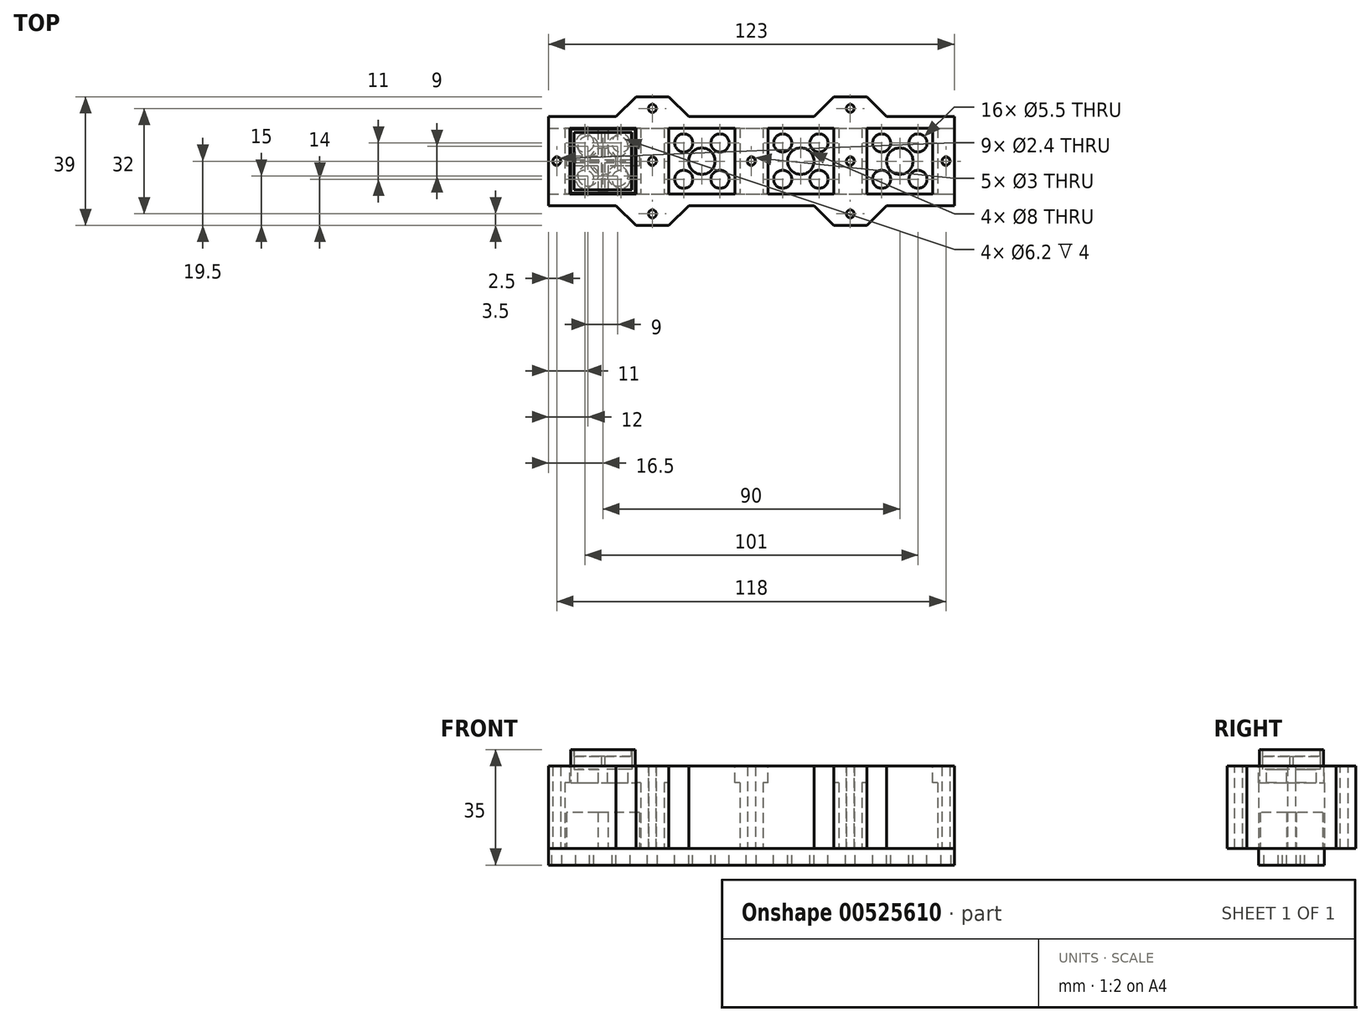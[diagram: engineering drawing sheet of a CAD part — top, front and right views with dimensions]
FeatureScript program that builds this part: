
annotation { "Feature Type Name" : "Feature", "Feature Type Description" : "" }
export const myFeature = defineFeature(function(context is Context, id is Id, definition is map)
    precondition{}
    {
        {
            var Q0;
            Q0=qCreatedBy(makeId("Top.planeOp"),FACE);
            var sketch = newSketch(context, id + "F0", { "sketchPlane" : qUnion([Q0])});
            skPoint(sketch, "E0.middle", {"position": v(0, 0) * mm});
            skLineSegment(sketch, "E1.bottom", {"start": v(9.75, -9.75) * mm, "end": v(-9.75, -9.75) * mm});
            skLineSegment(sketch, "E1.top", {"start": v(9.75, 9.75) * mm, "end": v(-9.75, 9.75) * mm});
            skLineSegment(sketch, "E1.left", {"start": v(9.75, -9.75) * mm, "end": v(9.75, 9.75) * mm});
            skLineSegment(sketch, "E1.right", {"start": v(-9.75, -9.75) * mm, "end": v(-9.75, 9.75) * mm});
            skSolve(sketch);
        }
        {
            var Q0;
            Q0=qSketchRegion(id+"F0",true);
            extrude(context, id + "F1", {"entities" : qUnion([Q0]), "depth" : 13 * mm, "offsetDistance" : 25 * mm});
        }
        {
            var Q0;
            Q0=makeQuery(id+"F1.opExtrude","CAP_FACE",FACE,{"disambiguationData":[OSD([sQuery(id+"F0.wireOp",EDGE,"E1.bottom"),sQuery(id+"F0.wireOp",EDGE,"E1.top"),sQuery(id+"F0.wireOp",EDGE,"E1.left"),sQuery(id+"F0.wireOp",EDGE,"E1.right")])],"isStart":false});
            var sketch = newSketch(context, id + "F2", { "sketchPlane" : qUnion([Q0])});
            skLineSegment(sketch, "E2.bottom", {"start": v(9.75, -9.75) * mm, "end": v(-9.75, -9.75) * mm});
            skLineSegment(sketch, "E2.top", {"start": v(9.75, 9.75) * mm, "end": v(-9.75, 9.75) * mm});
            skLineSegment(sketch, "E2.left", {"start": v(9.75, -9.75) * mm, "end": v(9.75, 9.75) * mm});
            skLineSegment(sketch, "E2.right", {"start": v(-9.75, -9.75) * mm, "end": v(-9.75, 9.75) * mm});
            skPoint(sketch, "E2.middle", {"position": v(0, 0) * mm});
            skLineSegment(sketch, "E3.bottom", {"start": v(8.75, -8.75) * mm, "end": v(-8.75, -8.75) * mm});
            skLineSegment(sketch, "E3.top", {"start": v(8.75, 8.75) * mm, "end": v(-8.75, 8.75) * mm});
            skLineSegment(sketch, "E3.left", {"start": v(8.75, -8.75) * mm, "end": v(8.75, 8.75) * mm});
            skLineSegment(sketch, "E3.right", {"start": v(-8.75, -8.75) * mm, "end": v(-8.75, 8.75) * mm});
            skSolve(sketch);
        }
        {
            var Q0;
            Q0=qSketchRegion(id+"F2",true);
            extrude(context, id + "F3", {"entities" : qUnion([Q0]), "operationType" : NewBodyOperationType.ADD, "depth" : 6 * mm, "offsetDistance" : 25 * mm});
        }
        {
            var Q0;
            Q0=makeQuery(id+"F1.opExtrude","CAP_FACE",FACE,{"disambiguationData":[OSD([sQuery(id+"F0.wireOp",EDGE,"E1.bottom"),sQuery(id+"F0.wireOp",EDGE,"E1.top"),sQuery(id+"F0.wireOp",EDGE,"E1.left"),sQuery(id+"F0.wireOp",EDGE,"E1.right")])],"isStart":false});
            var sketch = newSketch(context, id + "F4", { "sketchPlane" : qUnion([Q0])});
            skLineSegment(sketch, "E4.bottom", {"start": v(-0.5, 8.75) * mm, "end": v(0.5, 8.75) * mm});
            skLineSegment(sketch, "E4.top", {"start": v(-0.5, -8.75) * mm, "end": v(0.5, -8.75) * mm});
            skLineSegment(sketch, "E4.left", {"start": v(-0.5, 8.75) * mm, "end": v(-0.5, 0.5) * mm});
            skLineSegment(sketch, "E4.right", {"start": v(0.5, 8.75) * mm, "end": v(0.5, 0.5) * mm});
            skLineSegment(sketch, "E5.bottom", {"start": v(-8.75, 0.5) * mm, "end": v(-0.5, 0.5) * mm});
            skLineSegment(sketch, "E5.top", {"start": v(-8.75, -0.5) * mm, "end": v(-0.5, -0.5) * mm});
            skLineSegment(sketch, "E5.left", {"start": v(-8.75, 0.5) * mm, "end": v(-8.75, -0.5) * mm});
            skLineSegment(sketch, "E5.right", {"start": v(8.75, 0.5) * mm, "end": v(8.75, -0.5) * mm});
            skLineSegment(sketch, "E6.trimOffspring", {"start": v(-0.5, -0.5) * mm, "end": v(-0.5, -8.75) * mm});
            skLineSegment(sketch, "E7.trimOffspring", {"start": v(0.5, -0.5) * mm, "end": v(0.5, -8.75) * mm});
            skLineSegment(sketch, "E8.trimOffspring", {"start": v(0.5, 0.5) * mm, "end": v(8.75, 0.5) * mm});
            skLineSegment(sketch, "E9.trimOffspring", {"start": v(0.5, -0.5) * mm, "end": v(8.75, -0.5) * mm});
            skSolve(sketch);
        }
        {
            var Q0;
            Q0=qSketchRegion(id+"F4",true);
            extrude(context, id + "F5", {"entities" : qUnion([Q0]), "operationType" : NewBodyOperationType.ADD, "depth" : 4 * mm, "offsetDistance" : 25 * mm});
        }
        {
            var Q0;
            Q0=makeQuery(id+"F1.opExtrude","CAP_FACE",FACE,{"disambiguationData":[OSD([sQuery(id+"F0.wireOp",EDGE,"E1.bottom"),sQuery(id+"F0.wireOp",EDGE,"E1.top"),sQuery(id+"F0.wireOp",EDGE,"E1.left"),sQuery(id+"F0.wireOp",EDGE,"E1.right")])],"isStart":false});
            var sketch = newSketch(context, id + "F6", { "sketchPlane" : qUnion([Q0])});
            skCircle(sketch, "E10", {"center": v(-4.5, 4.5) * mm, "radius": 3.1 * mm});
            skCircle(sketch, "E11", {"center": v(-4.5, -4.5) * mm, "radius": 3.1 * mm});
            skCircle(sketch, "E12", {"center": v(4.5, 4.5) * mm, "radius": 3.1 * mm});
            skCircle(sketch, "E13", {"center": v(4.5, -4.5) * mm, "radius": 3.1 * mm});
            skSolve(sketch);
        }
        {
            var Q0;
            Q0=qSketchRegion(id+"F6",true);
            extrude(context, id + "F7", {"entities" : qUnion([Q0]), "operationType" : NewBodyOperationType.REMOVE, "oppositeDirection" : true, "depth" : 19 * mm, "offsetDistance" : 25 * mm});
        }
        {
            var Q0;
            Q0=makeQuery(id+"F1.opExtrude","CAP_FACE",FACE,{"disambiguationData":[OSD([sQuery(id+"F0.wireOp",EDGE,"E1.bottom"),sQuery(id+"F0.wireOp",EDGE,"E1.top"),sQuery(id+"F0.wireOp",EDGE,"E1.left"),sQuery(id+"F0.wireOp",EDGE,"E1.right")])],"isStart":true});
            var sketch = newSketch(context, id + "F8", { "sketchPlane" : qUnion([Q0])});
            skLineSegment(sketch, "E14.bottom", {"start": v(-9.75, -9.75) * mm, "end": v(-11.25, -9.75) * mm});
            skLineSegment(sketch, "E14.top", {"start": v(-9.75, 9.75) * mm, "end": v(-11.25, 9.75) * mm});
            skLineSegment(sketch, "E14.left", {"start": v(-9.75, -9.75) * mm, "end": v(-9.75, 9.75) * mm});
            skLineSegment(sketch, "E14.right", {"start": v(-11.25, -9.75) * mm, "end": v(-11.25, 9.75) * mm});
            skLineSegment(sketch, "E15.bottom", {"start": v(9.75, -9.75) * mm, "end": v(11.25, -9.75) * mm});
            skLineSegment(sketch, "E15.top", {"start": v(9.75, 9.75) * mm, "end": v(11.25, 9.75) * mm});
            skLineSegment(sketch, "E15.left", {"start": v(9.75, -9.75) * mm, "end": v(9.75, 9.75) * mm});
            skLineSegment(sketch, "E15.right", {"start": v(11.25, -9.75) * mm, "end": v(11.25, 9.75) * mm});
            skSolve(sketch);
        }
        {
            var Q0;
            Q0=qSketchRegion(id+"F8",true);
            extrude(context, id + "F9", {"entities" : qUnion([Q0]), "operationType" : NewBodyOperationType.ADD, "oppositeDirection" : true, "depth" : 9 * mm, "offsetDistance" : 25 * mm});
        }
        {
            var Q0;
            Q0=makeQuery(id+"F9.boolean.opBoolean","MERGE",FACE,{"derivedFrom":[makeQuery(id+"F1.opExtrude","CAP_FACE",FACE,{"disambiguationData":[OSD([sQuery(id+"F0.wireOp",EDGE,"E1.bottom"),sQuery(id+"F0.wireOp",EDGE,"E1.top"),sQuery(id+"F0.wireOp",EDGE,"E1.left"),sQuery(id+"F0.wireOp",EDGE,"E1.right")])],"isStart":true}),makeQuery(id+"F9.opExtrude","CAP_FACE",FACE,{"disambiguationData":[OSD([sQuery(id+"F8.wireOp",EDGE,"E14.bottom"),sQuery(id+"F8.wireOp",EDGE,"E14.top"),sQuery(id+"F8.wireOp",EDGE,"E14.left"),sQuery(id+"F8.wireOp",EDGE,"E14.right")])],"isStart":true}),makeQuery(id+"F9.opExtrude","CAP_FACE",FACE,{"disambiguationData":[OSD([sQuery(id+"F8.wireOp",EDGE,"E15.bottom"),sQuery(id+"F8.wireOp",EDGE,"E15.top"),sQuery(id+"F8.wireOp",EDGE,"E15.left"),sQuery(id+"F8.wireOp",EDGE,"E15.right")])],"isStart":true})]});
            var sketch = newSketch(context, id + "F10", { "sketchPlane" : qUnion([Q0])});
            skCircle(sketch, "E16", {"center": v(0, 0) * mm, "radius": 2.55 * mm});
            skSolve(sketch);
        }
        {
            var Q0;
            Q0 = qSketchRegion(id + "F10", true);
            extrude(context, id + "F11", {"entities" : qUnion([Q0]), "operationType" : NewBodyOperationType.REMOVE, "oppositeDirection" : true, "depth" : 3 * mm, "offsetDistance" : 25 * mm});
        }
        {
            var Q0;
            Q0=qCreatedBy(makeId("Top.planeOp"),FACE);
            cPlane(context, id + "F12", {"entities" : qUnion([Q0]), "cplaneType" : CPlaneType.OFFSET, "offset" : 14 * mm, "width" : 150 * mm, "height" : 150 * mm});
        }
        {
            var Q0;
            Q0=qCreatedBy(id+"F12.planeOp",FACE);
            var sketch = newSketch(context, id + "F13", { "sketchPlane" : qUnion([Q0])});
            skPoint(sketch, "E17.middle", {"position": v(0, 0) * mm});
            skLineSegment(sketch, "E18.bottom", {"start": v(10, -10) * mm, "end": v(-10, -10) * mm});
            skLineSegment(sketch, "E18.top", {"start": v(10, 10) * mm, "end": v(-10, 10) * mm});
            skLineSegment(sketch, "E18.left", {"start": v(10, -10) * mm, "end": v(10, 10) * mm});
            skLineSegment(sketch, "E18.right", {"start": v(-10, -10) * mm, "end": v(-10, 10) * mm});
            skLineSegment(sketch, "E19.bottom", {"start": v(40, -10) * mm, "end": v(20, -10) * mm});
            skLineSegment(sketch, "E19.top", {"start": v(40, 10) * mm, "end": v(20, 10) * mm});
            skLineSegment(sketch, "E19.left", {"start": v(40, -10) * mm, "end": v(40, 10) * mm});
            skLineSegment(sketch, "E19.right", {"start": v(20, -10) * mm, "end": v(20, 10) * mm});
            skPoint(sketch, "E19.middle", {"position": v(30, 0) * mm});
            skLineSegment(sketch, "E20.bottom", {"start": v(70, -10) * mm, "end": v(50, -10) * mm});
            skLineSegment(sketch, "E20.top", {"start": v(70, 10) * mm, "end": v(50, 10) * mm});
            skLineSegment(sketch, "E20.left", {"start": v(70, -10) * mm, "end": v(70, 10) * mm});
            skLineSegment(sketch, "E20.right", {"start": v(50, -10) * mm, "end": v(50, 10) * mm});
            skPoint(sketch, "E20.middle", {"position": v(60, 0) * mm});
            skLineSegment(sketch, "E21.bottom", {"start": v(100, -10) * mm, "end": v(80, -10) * mm});
            skLineSegment(sketch, "E21.top", {"start": v(100, 10) * mm, "end": v(80, 10) * mm});
            skLineSegment(sketch, "E21.left", {"start": v(100, -10) * mm, "end": v(100, 10) * mm});
            skLineSegment(sketch, "E21.right", {"start": v(80, -10) * mm, "end": v(80, 10) * mm});
            skPoint(sketch, "E21.middle", {"position": v(90, 0) * mm});
            skLineSegment(sketch, "E22.bottom", {"start": v(10, 13.5) * mm, "end": v(20, 13.5) * mm});
            skLineSegment(sketch, "E22.top", {"start": v(10, 19.5) * mm, "end": v(20, 19.5) * mm});
            skLineSegment(sketch, "E22.left", {"start": v(10, 13.5) * mm, "end": v(10, 19.5) * mm});
            skLineSegment(sketch, "E22.right", {"start": v(20, 13.5) * mm, "end": v(20, 19.5) * mm});
            skLineSegment(sketch, "E23.bottom", {"start": v(10, -13.5) * mm, "end": v(20, -13.5) * mm});
            skLineSegment(sketch, "E23.top", {"start": v(10, -19.5) * mm, "end": v(20, -19.5) * mm});
            skLineSegment(sketch, "E23.left", {"start": v(10, -13.5) * mm, "end": v(10, -19.5) * mm});
            skLineSegment(sketch, "E23.right", {"start": v(20, -13.5) * mm, "end": v(20, -19.5) * mm});
            skLineSegment(sketch, "E24.bottom", {"start": v(106.5, -13.5) * mm, "end": v(-16.5, -13.5) * mm});
            skLineSegment(sketch, "E24.top", {"start": v(106.5, 13.5) * mm, "end": v(-16.5, 13.5) * mm});
            skLineSegment(sketch, "E24.left", {"start": v(106.5, -13.5) * mm, "end": v(106.5, 13.5) * mm});
            skLineSegment(sketch, "E24.right", {"start": v(-16.5, -13.5) * mm, "end": v(-16.5, 13.5) * mm});
            skPoint(sketch, "E24.middle", {"position": v(45, 0) * mm});
            skLineSegment(sketch, "E25.bottom", {"start": v(70, 13.5) * mm, "end": v(80, 13.5) * mm});
            skLineSegment(sketch, "E25.top", {"start": v(70, 19.5) * mm, "end": v(80, 19.5) * mm});
            skLineSegment(sketch, "E25.left", {"start": v(70, 13.5) * mm, "end": v(70, 19.5) * mm});
            skLineSegment(sketch, "E25.right", {"start": v(80, 13.5) * mm, "end": v(80, 19.5) * mm});
            skLineSegment(sketch, "E26.bottom", {"start": v(70, -13.5) * mm, "end": v(80, -13.5) * mm});
            skLineSegment(sketch, "E26.top", {"start": v(70, -19.5) * mm, "end": v(80, -19.5) * mm});
            skLineSegment(sketch, "E26.left", {"start": v(70, -13.5) * mm, "end": v(70, -19.5) * mm});
            skLineSegment(sketch, "E26.right", {"start": v(80, -13.5) * mm, "end": v(80, -19.5) * mm});
            skSolve(sketch);
        }
        {
            var Q0;
            Q0=qSketchRegion(id+"F13",true);
            extrude(context, id + "F14", {"entities" : qUnion([Q0]), "oppositeDirection" : true, "depth" : 25 * mm, "offsetDistance" : 25 * mm});
        }
        {
            var Q0;
            Q0=makeQuery(id+"F14.opExtrude","CAP_FACE",FACE,{"disambiguationData":[OSD([sQuery(id+"F13.wireOp",EDGE,"E17.bottom"),sQuery(id+"F13.wireOp",EDGE,"E17.top"),sQuery(id+"F13.wireOp",EDGE,"E17.left"),sQuery(id+"F13.wireOp",EDGE,"E17.right"),sQuery(id+"F13.wireOp",EDGE,"E18.bottom"),sQuery(id+"F13.wireOp",EDGE,"E18.top"),sQuery(id+"F13.wireOp",EDGE,"E18.left"),sQuery(id+"F13.wireOp",EDGE,"E18.right")])],"isStart":false});
            var sketch = newSketch(context, id + "F15", { "sketchPlane" : qUnion([Q0])});
            skLineSegment(sketch, "E27.bottom", {"start": v(11.5, -10) * mm, "end": v(-11.5, -10) * mm});
            skLineSegment(sketch, "E27.top", {"start": v(11.5, 10) * mm, "end": v(-11.5, 10) * mm});
            skLineSegment(sketch, "E27.left", {"start": v(11.5, -10) * mm, "end": v(11.5, 10) * mm});
            skLineSegment(sketch, "E27.right", {"start": v(-11.5, -10) * mm, "end": v(-11.5, 10) * mm});
            skPoint(sketch, "E27.middle", {"position": v(0, 0) * mm});
            skLineSegment(sketch, "E28.bottom", {"start": v(41.5, -10) * mm, "end": v(18.5, -10) * mm});
            skLineSegment(sketch, "E28.top", {"start": v(41.5, 10) * mm, "end": v(18.5, 10) * mm});
            skLineSegment(sketch, "E28.left", {"start": v(41.5, -10) * mm, "end": v(41.5, 10) * mm});
            skLineSegment(sketch, "E28.right", {"start": v(18.5, -10) * mm, "end": v(18.5, 10) * mm});
            skPoint(sketch, "E28.middle", {"position": v(30, 0) * mm});
            skPoint(sketch, "E28.middle.positionSnap0", {"position": v(20, 0) * mm});
            skPoint(sketch, "E28.middle.positionSnap1", {"position": v(30, 10) * mm});
            skPoint(sketch, "E28.centerSnap0", {"position": v(20, 0) * mm});
            skPoint(sketch, "E28.centerSnap1", {"position": v(30, 10) * mm});
            skLineSegment(sketch, "E29.bottom", {"start": v(71.5, -10) * mm, "end": v(48.5, -10) * mm});
            skLineSegment(sketch, "E29.top", {"start": v(71.5, 10) * mm, "end": v(48.5, 10) * mm});
            skLineSegment(sketch, "E29.left", {"start": v(71.5, -10) * mm, "end": v(71.5, 10) * mm});
            skLineSegment(sketch, "E29.right", {"start": v(48.5, -10) * mm, "end": v(48.5, 10) * mm});
            skPoint(sketch, "E29.middle", {"position": v(60, 0) * mm});
            skPoint(sketch, "E29.middle.positionSnap0", {"position": v(50, 0) * mm});
            skPoint(sketch, "E29.middle.positionSnap1", {"position": v(60, 10) * mm});
            skPoint(sketch, "E29.centerSnap0", {"position": v(50, 0) * mm});
            skPoint(sketch, "E29.centerSnap1", {"position": v(60, 10) * mm});
            skLineSegment(sketch, "E30.bottom", {"start": v(101.5, -10) * mm, "end": v(78.5, -10) * mm});
            skLineSegment(sketch, "E30.top", {"start": v(101.5, 10) * mm, "end": v(78.5, 10) * mm});
            skLineSegment(sketch, "E30.left", {"start": v(101.5, -10) * mm, "end": v(101.5, 10) * mm});
            skLineSegment(sketch, "E30.right", {"start": v(78.5, -10) * mm, "end": v(78.5, 10) * mm});
            skPoint(sketch, "E30.middle", {"position": v(90, 0) * mm});
            skPoint(sketch, "E30.middle.positionSnap0", {"position": v(90, 10) * mm});
            skPoint(sketch, "E30.centerSnap0", {"position": v(90, 10) * mm});
            skSolve(sketch);
        }
        {
            var Q0;
            Q0=qSketchRegion(id+"F15",true);
            extrude(context, id + "F16", {"entities" : qUnion([Q0]), "operationType" : NewBodyOperationType.REMOVE, "oppositeDirection" : true, "depth" : 20 * mm, "offsetDistance" : 25 * mm});
        }
        {
            var Q0;
            Q0=makeQuery(id+"F14.opExtrude","CAP_FACE",FACE,{"disambiguationData":[OSD([sQuery(id+"F13.wireOp",EDGE,"E18.bottom"),sQuery(id+"F13.wireOp",EDGE,"E18.top"),sQuery(id+"F13.wireOp",EDGE,"E18.left"),sQuery(id+"F13.wireOp",EDGE,"E18.right"),sQuery(id+"F13.wireOp",EDGE,"E19.bottom"),sQuery(id+"F13.wireOp",EDGE,"E19.top"),sQuery(id+"F13.wireOp",EDGE,"E19.left"),sQuery(id+"F13.wireOp",EDGE,"E19.right"),sQuery(id+"F13.wireOp",EDGE,"E20.bottom"),sQuery(id+"F13.wireOp",EDGE,"E20.top"),sQuery(id+"F13.wireOp",EDGE,"E20.left"),sQuery(id+"F13.wireOp",EDGE,"E20.right"),sQuery(id+"F13.wireOp",EDGE,"E21.bottom"),sQuery(id+"F13.wireOp",EDGE,"E21.top"),sQuery(id+"F13.wireOp",EDGE,"E21.left"),sQuery(id+"F13.wireOp",EDGE,"E21.right"),sQuery(id+"F13.wireOp",EDGE,"E22.top"),sQuery(id+"F13.wireOp",EDGE,"E22.left"),sQuery(id+"F13.wireOp",EDGE,"E22.right"),sQuery(id+"F13.wireOp",EDGE,"E23.top"),sQuery(id+"F13.wireOp",EDGE,"E23.left"),sQuery(id+"F13.wireOp",EDGE,"E23.right"),sQuery(id+"F13.wireOp",EDGE,"E24.bottom"),sQuery(id+"F13.wireOp",EDGE,"E24.top"),sQuery(id+"F13.wireOp",EDGE,"E24.left"),sQuery(id+"F13.wireOp",EDGE,"E24.right"),sQuery(id+"F13.wireOp",EDGE,"E25.top"),sQuery(id+"F13.wireOp",EDGE,"E25.left"),sQuery(id+"F13.wireOp",EDGE,"E25.right"),sQuery(id+"F13.wireOp",EDGE,"E26.top"),sQuery(id+"F13.wireOp",EDGE,"E26.left"),sQuery(id+"F13.wireOp",EDGE,"E26.right")])],"isStart":true});
            var sketch = newSketch(context, id + "F17", { "sketchPlane" : qUnion([Q0])});
            skCircle(sketch, "E31", {"center": v(15, 16) * mm, "radius": 1.2 * mm});
            skPoint(sketch, "E31.centerSnap0", {"position": v(15, 19.5) * mm});
            skCircle(sketch, "E32", {"center": v(15, -16) * mm, "radius": 1.2 * mm});
            skCircle(sketch, "E33", {"center": v(75, 16) * mm, "radius": 1.2 * mm});
            skPoint(sketch, "E33.centerSnap0", {"position": v(75, 19.5) * mm});
            skCircle(sketch, "E34", {"center": v(75, -16) * mm, "radius": 1.2 * mm});
            skSolve(sketch);
        }
        {
            var Q0;
            Q0 = qSketchRegion(id + "F17", true);
            extrude(context, id + "F18", {"entities" : qUnion([Q0]), "operationType" : NewBodyOperationType.REMOVE, "oppositeDirection" : true, "depth" : 30 * mm, "offsetDistance" : 25 * mm});
        }
        {
            var Q0;
            Q0=makeQuery(id+"F14.opExtrude","CAP_FACE",FACE,{"disambiguationData":[OSD([sQuery(id+"F13.wireOp",EDGE,"E18.bottom"),sQuery(id+"F13.wireOp",EDGE,"E18.top"),sQuery(id+"F13.wireOp",EDGE,"E18.left"),sQuery(id+"F13.wireOp",EDGE,"E18.right"),sQuery(id+"F13.wireOp",EDGE,"E19.bottom"),sQuery(id+"F13.wireOp",EDGE,"E19.top"),sQuery(id+"F13.wireOp",EDGE,"E19.left"),sQuery(id+"F13.wireOp",EDGE,"E19.right"),sQuery(id+"F13.wireOp",EDGE,"E20.bottom"),sQuery(id+"F13.wireOp",EDGE,"E20.top"),sQuery(id+"F13.wireOp",EDGE,"E20.left"),sQuery(id+"F13.wireOp",EDGE,"E20.right"),sQuery(id+"F13.wireOp",EDGE,"E21.bottom"),sQuery(id+"F13.wireOp",EDGE,"E21.top"),sQuery(id+"F13.wireOp",EDGE,"E21.left"),sQuery(id+"F13.wireOp",EDGE,"E21.right"),sQuery(id+"F13.wireOp",EDGE,"E22.top"),sQuery(id+"F13.wireOp",EDGE,"E22.left"),sQuery(id+"F13.wireOp",EDGE,"E22.right"),sQuery(id+"F13.wireOp",EDGE,"E23.top"),sQuery(id+"F13.wireOp",EDGE,"E23.left"),sQuery(id+"F13.wireOp",EDGE,"E23.right"),sQuery(id+"F13.wireOp",EDGE,"E24.bottom"),sQuery(id+"F13.wireOp",EDGE,"E24.top"),sQuery(id+"F13.wireOp",EDGE,"E24.left"),sQuery(id+"F13.wireOp",EDGE,"E24.right"),sQuery(id+"F13.wireOp",EDGE,"E25.top"),sQuery(id+"F13.wireOp",EDGE,"E25.left"),sQuery(id+"F13.wireOp",EDGE,"E25.right"),sQuery(id+"F13.wireOp",EDGE,"E26.top"),sQuery(id+"F13.wireOp",EDGE,"E26.left"),sQuery(id+"F13.wireOp",EDGE,"E26.right")])],"isStart":false});
            var sketch = newSketch(context, id + "F19", { "sketchPlane" : qUnion([Q0])});
            skCircle(sketch, "E35", {"center": v(-14, 0) * mm, "radius": 1.2 * mm});
            skCircle(sketch, "E36", {"center": v(15, 0) * mm, "radius": 1.2 * mm});
            skCircle(sketch, "E37", {"center": v(45, 0) * mm, "radius": 1.2 * mm});
            skCircle(sketch, "E38", {"center": v(75, 0) * mm, "radius": 1.2 * mm});
            skCircle(sketch, "E39", {"center": v(104, 0) * mm, "radius": 1.2 * mm});
            skSolve(sketch);
        }
        {
            var Q0;
            Q0 = qSketchRegion(id + "F19", true);
            extrude(context, id + "F20", {"entities" : qUnion([Q0]), "operationType" : NewBodyOperationType.REMOVE, "endBound" : BoundingType.THROUGH_ALL, "oppositeDirection" : true, "depth" : 10 * mm, "offsetDistance" : 25 * mm});
        }
        {
            var Q0;
            Q0=makeQuery(id+"F14.opExtrude","CAP_FACE",FACE,{"disambiguationData":[OSD([sQuery(id+"F13.wireOp",EDGE,"E18.bottom"),sQuery(id+"F13.wireOp",EDGE,"E18.top"),sQuery(id+"F13.wireOp",EDGE,"E18.left"),sQuery(id+"F13.wireOp",EDGE,"E18.right"),sQuery(id+"F13.wireOp",EDGE,"E19.bottom"),sQuery(id+"F13.wireOp",EDGE,"E19.top"),sQuery(id+"F13.wireOp",EDGE,"E19.left"),sQuery(id+"F13.wireOp",EDGE,"E19.right"),sQuery(id+"F13.wireOp",EDGE,"E20.bottom"),sQuery(id+"F13.wireOp",EDGE,"E20.top"),sQuery(id+"F13.wireOp",EDGE,"E20.left"),sQuery(id+"F13.wireOp",EDGE,"E20.right"),sQuery(id+"F13.wireOp",EDGE,"E21.bottom"),sQuery(id+"F13.wireOp",EDGE,"E21.top"),sQuery(id+"F13.wireOp",EDGE,"E21.left"),sQuery(id+"F13.wireOp",EDGE,"E21.right"),sQuery(id+"F13.wireOp",EDGE,"E22.top"),sQuery(id+"F13.wireOp",EDGE,"E22.left"),sQuery(id+"F13.wireOp",EDGE,"E22.right"),sQuery(id+"F13.wireOp",EDGE,"E23.top"),sQuery(id+"F13.wireOp",EDGE,"E23.left"),sQuery(id+"F13.wireOp",EDGE,"E23.right"),sQuery(id+"F13.wireOp",EDGE,"E24.bottom"),sQuery(id+"F13.wireOp",EDGE,"E24.top"),sQuery(id+"F13.wireOp",EDGE,"E24.left"),sQuery(id+"F13.wireOp",EDGE,"E24.right"),sQuery(id+"F13.wireOp",EDGE,"E25.top"),sQuery(id+"F13.wireOp",EDGE,"E25.left"),sQuery(id+"F13.wireOp",EDGE,"E25.right"),sQuery(id+"F13.wireOp",EDGE,"E26.top"),sQuery(id+"F13.wireOp",EDGE,"E26.left"),sQuery(id+"F13.wireOp",EDGE,"E26.right")])],"isStart":false});
            var sketch = newSketch(context, id + "F21", { "sketchPlane" : qUnion([Q0])});
            skCircle(sketch, "E40", {"center": v(-14, 0) * mm, "radius": 1.5 * mm});
            skCircle(sketch, "E41", {"center": v(15, 0) * mm, "radius": 1.5 * mm});
            skCircle(sketch, "E42", {"center": v(45, 0) * mm, "radius": 1.5 * mm});
            skCircle(sketch, "E43", {"center": v(75, 0) * mm, "radius": 1.5 * mm});
            skCircle(sketch, "E44", {"center": v(104, 0) * mm, "radius": 1.5 * mm});
            skCircle(sketch, "E45", {"center": v(0, 0) * mm, "radius": 4 * mm});
            skCircle(sketch, "E46", {"center": v(-5.5, 5.5) * mm, "radius": 2.75 * mm});
            skCircle(sketch, "E47", {"center": v(5.5, 5.5) * mm, "radius": 2.75 * mm});
            skCircle(sketch, "E48", {"center": v(-5.5, -5.5) * mm, "radius": 2.75 * mm});
            skCircle(sketch, "E49", {"center": v(5.5, -5.5) * mm, "radius": 2.75 * mm});
            skCircle(sketch, "E50.1.0.0", {"center": v(30, 0) * mm, "radius": 4 * mm});
            skCircle(sketch, "E50.1.0.1", {"center": v(35.5, -5.5) * mm, "radius": 2.75 * mm});
            skCircle(sketch, "E50.1.0.2", {"center": v(35.5, 5.5) * mm, "radius": 2.75 * mm});
            skCircle(sketch, "E50.1.0.3", {"center": v(24.5, 5.5) * mm, "radius": 2.75 * mm});
            skCircle(sketch, "E50.1.0.4", {"center": v(24.5, -5.5) * mm, "radius": 2.75 * mm});
            skCircle(sketch, "E50.2.0.0", {"center": v(60, 0) * mm, "radius": 4 * mm});
            skCircle(sketch, "E50.2.0.1", {"center": v(65.5, -5.5) * mm, "radius": 2.75 * mm});
            skCircle(sketch, "E50.2.0.2", {"center": v(65.5, 5.5) * mm, "radius": 2.75 * mm});
            skCircle(sketch, "E50.2.0.3", {"center": v(54.5, 5.5) * mm, "radius": 2.75 * mm});
            skCircle(sketch, "E50.2.0.4", {"center": v(54.5, -5.5) * mm, "radius": 2.75 * mm});
            skLineSegment(sketch, "E50.direction1", {"start": v(-5.5, -5.5) * mm, "end": v(24.5, -5.5) * mm, "construction": true});
            skCircle(sketch, "E51.0.3.0", {"center": v(90, 0) * mm, "radius": 4 * mm});
            skCircle(sketch, "E51.2.3.0", {"center": v(95.5, -5.5) * mm, "radius": 2.75 * mm});
            skCircle(sketch, "E51.4.3.0", {"center": v(95.5, 5.5) * mm, "radius": 2.75 * mm});
            skCircle(sketch, "E51.6.3.0", {"center": v(84.5, 5.5) * mm, "radius": 2.75 * mm});
            skCircle(sketch, "E51.8.3.0", {"center": v(84.5, -5.5) * mm, "radius": 2.75 * mm});
            skLineSegment(sketch, "E52.bottom", {"start": v(-16.5, -10) * mm, "end": v(106.5, -10) * mm});
            skLineSegment(sketch, "E52.top", {"start": v(-16.5, 10) * mm, "end": v(106.5, 10) * mm});
            skLineSegment(sketch, "E52.left", {"start": v(-16.5, -10) * mm, "end": v(-16.5, 10) * mm});
            skLineSegment(sketch, "E52.right", {"start": v(106.5, -10) * mm, "end": v(106.5, 10) * mm});
            skSolve(sketch);
        }
        {
            var Q0;
            Q0 = qSketchRegion(id + "F21", true);
            extrude(context, id + "F22", {"entities" : qUnion([Q0]), "depth" : 5 * mm, "offsetDistance" : 25 * mm});
        }
        {
            var Q0;
            Q0=makeQuery(id+"F14.opExtrude","SWEPT_EDGE",EDGE,{"disambiguationData":[OSD([sQuery(id+"F13.wireOp",EDGE,"E23.left"),sQuery(id+"F13.wireOp",EDGE,"E24.bottom")])]});
            var Q1;
            Q1=makeQuery(id+"F14.opExtrude","SWEPT_EDGE",EDGE,{"disambiguationData":[OSD([sQuery(id+"F13.wireOp",EDGE,"E23.right"),sQuery(id+"F13.wireOp",EDGE,"E24.bottom")])]});
            var Q2;
            Q2=makeQuery(id+"F14.opExtrude","SWEPT_EDGE",EDGE,{"disambiguationData":[OSD([sQuery(id+"F13.wireOp",EDGE,"E24.bottom"),sQuery(id+"F13.wireOp",EDGE,"E26.bottom"),sQuery(id+"F13.wireOp",EDGE,"E26.left")])]});
            var Q3;
            Q3=makeQuery(id+"F14.opExtrude","SWEPT_EDGE",EDGE,{"disambiguationData":[OSD([sQuery(id+"F13.wireOp",EDGE,"E24.bottom"),sQuery(id+"F13.wireOp",EDGE,"E26.bottom"),sQuery(id+"F13.wireOp",EDGE,"E26.right")])]});
            var Q4;
            Q4=makeQuery(id+"F14.opExtrude","SWEPT_EDGE",EDGE,{"disambiguationData":[OSD([sQuery(id+"F13.wireOp",EDGE,"E22.left"),sQuery(id+"F13.wireOp",EDGE,"E24.top")])]});
            var Q5;
            Q5=makeQuery(id+"F14.opExtrude","SWEPT_EDGE",EDGE,{"disambiguationData":[OSD([sQuery(id+"F13.wireOp",EDGE,"E22.right"),sQuery(id+"F13.wireOp",EDGE,"E24.top")])]});
            var Q6;
            Q6=makeQuery(id+"F14.opExtrude","SWEPT_EDGE",EDGE,{"disambiguationData":[OSD([sQuery(id+"F13.wireOp",EDGE,"E24.top"),sQuery(id+"F13.wireOp",EDGE,"E25.bottom"),sQuery(id+"F13.wireOp",EDGE,"E25.left")])]});
            var Q7;
            Q7=makeQuery(id+"F14.opExtrude","SWEPT_EDGE",EDGE,{"disambiguationData":[OSD([sQuery(id+"F13.wireOp",EDGE,"E24.top"),sQuery(id+"F13.wireOp",EDGE,"E25.bottom"),sQuery(id+"F13.wireOp",EDGE,"E25.right")])]});
            chamfer(context, id + "F23", {"entities" : qUnion([Q0, Q1, Q2, Q3, Q4, Q5, Q6, Q7]), "width" : 6 * mm, "tangentPropagation" : true});
        }
        {
            var Q0;
            Q0=makeQuery(id+"F14.opExtrude","CAP_FACE",FACE,{"disambiguationData":[OSD([sQuery(id+"F13.wireOp",EDGE,"E18.bottom"),sQuery(id+"F13.wireOp",EDGE,"E18.top"),sQuery(id+"F13.wireOp",EDGE,"E18.left"),sQuery(id+"F13.wireOp",EDGE,"E18.right"),sQuery(id+"F13.wireOp",EDGE,"E19.bottom"),sQuery(id+"F13.wireOp",EDGE,"E19.top"),sQuery(id+"F13.wireOp",EDGE,"E19.left"),sQuery(id+"F13.wireOp",EDGE,"E19.right"),sQuery(id+"F13.wireOp",EDGE,"E20.bottom"),sQuery(id+"F13.wireOp",EDGE,"E20.top"),sQuery(id+"F13.wireOp",EDGE,"E20.left"),sQuery(id+"F13.wireOp",EDGE,"E20.right"),sQuery(id+"F13.wireOp",EDGE,"E21.bottom"),sQuery(id+"F13.wireOp",EDGE,"E21.top"),sQuery(id+"F13.wireOp",EDGE,"E21.left"),sQuery(id+"F13.wireOp",EDGE,"E21.right"),sQuery(id+"F13.wireOp",EDGE,"E22.top"),sQuery(id+"F13.wireOp",EDGE,"E22.left"),sQuery(id+"F13.wireOp",EDGE,"E22.right"),sQuery(id+"F13.wireOp",EDGE,"E23.top"),sQuery(id+"F13.wireOp",EDGE,"E23.left"),sQuery(id+"F13.wireOp",EDGE,"E23.right"),sQuery(id+"F13.wireOp",EDGE,"E24.bottom"),sQuery(id+"F13.wireOp",EDGE,"E24.top"),sQuery(id+"F13.wireOp",EDGE,"E24.left"),sQuery(id+"F13.wireOp",EDGE,"E24.right"),sQuery(id+"F13.wireOp",EDGE,"E25.top"),sQuery(id+"F13.wireOp",EDGE,"E25.left"),sQuery(id+"F13.wireOp",EDGE,"E25.right"),sQuery(id+"F13.wireOp",EDGE,"E26.top"),sQuery(id+"F13.wireOp",EDGE,"E26.left"),sQuery(id+"F13.wireOp",EDGE,"E26.right")])],"isStart":false});
            cPlane(context, id + "F24", {"entities" : qUnion([Q0]), "cplaneType" : CPlaneType.OFFSET, "offset" : 0 * mm, "width" : 150 * mm, "height" : 150 * mm});
        }
        {
            var Q0;
            Q0=qCreatedBy(id+"F24.planeOp",FACE);
            var sketch = newSketch(context, id + "F25", { "sketchPlane" : qUnion([Q0])});
            skLineSegment(sketch, "E53.bottom", {"start": v(1.5, -9.5) * mm, "end": v(-1.5, -9.5) * mm});
            skLineSegment(sketch, "E53.top", {"start": v(1.5, 9.5) * mm, "end": v(-1.5, 9.5) * mm});
            skLineSegment(sketch, "E53.left", {"start": v(1.5, -9.5) * mm, "end": v(1.5, 9.5) * mm});
            skLineSegment(sketch, "E53.right", {"start": v(-1.5, -9.5) * mm, "end": v(-1.5, 9.5) * mm});
            skPoint(sketch, "E53.middle", {"position": v(0, 0) * mm});
            skLineSegment(sketch, "E54.bottom", {"start": v(11, -1.5) * mm, "end": v(-11, -1.5) * mm});
            skLineSegment(sketch, "E54.top", {"start": v(11, 1.5) * mm, "end": v(-11, 1.5) * mm});
            skLineSegment(sketch, "E54.left", {"start": v(11, -1.5) * mm, "end": v(11, 1.5) * mm});
            skLineSegment(sketch, "E54.right", {"start": v(-11, -1.5) * mm, "end": v(-11, 1.5) * mm});
            skLineSegment(sketch, "E55.0", {"start": v(11.5, 10) * mm, "end": v(-11.5, 10) * mm});
            skLineSegment(sketch, "E55.1", {"start": v(11.5, -10) * mm, "end": v(11.5, 10) * mm});
            skPoint(sketch, "E56", {"position": v(11.5, 0) * mm});
            skPoint(sketch, "E57", {"position": v(0, 10) * mm});
            skSolve(sketch);
        }
        {
            var Q0;
            Q0 = qSketchRegion(id + "F25", true);
            extrude(context, id + "F26", {"entities" : qUnion([Q0]), "oppositeDirection" : true, "depth" : 11 * mm, "offsetDistance" : 25 * mm});
        }
        {
            var Q0;
            Q0=makeQuery(id+"F3.opExtrude","CAP_FACE",FACE,{"disambiguationData":[OSD([sQuery(id+"F2.wireOp",EDGE,"E2.bottom"),sQuery(id+"F2.wireOp",EDGE,"E2.top"),sQuery(id+"F2.wireOp",EDGE,"E2.left"),sQuery(id+"F2.wireOp",EDGE,"E2.right"),sQuery(id+"F2.wireOp",EDGE,"E3.bottom"),sQuery(id+"F2.wireOp",EDGE,"E3.top"),sQuery(id+"F2.wireOp",EDGE,"E3.left"),sQuery(id+"F2.wireOp",EDGE,"E3.right")])],"isStart":false});
            var sketch = newSketch(context, id + "F27", { "sketchPlane" : qUnion([Q0])});
            skLineSegment(sketch, "E58.bottom", {"start": v(8.7, -8.7) * mm, "end": v(-8.7, -8.7) * mm});
            skLineSegment(sketch, "E58.top", {"start": v(8.7, 8.7) * mm, "end": v(-8.7, 8.7) * mm});
            skLineSegment(sketch, "E58.left", {"start": v(8.7, -8.7) * mm, "end": v(8.7, 8.7) * mm});
            skLineSegment(sketch, "E58.right", {"start": v(-8.7, -8.7) * mm, "end": v(-8.7, 8.7) * mm});
            skPoint(sketch, "E58.middle", {"position": v(0, 0) * mm});
            skPoint(sketch, "E58.middle.positionSnap0", {"position": v(-8.75, 0) * mm});
            skPoint(sketch, "E58.middle.positionSnap1", {"position": v(0, 8.75) * mm});
            skPoint(sketch, "E58.centerSnap0", {"position": v(-8.75, 0) * mm});
            skPoint(sketch, "E58.centerSnap1", {"position": v(0, 8.75) * mm});
            skSolve(sketch);
        }
        {
            var Q0;
            Q0 = qSketchRegion(id + "F27", true);
            extrude(context, id + "F28", {"entities" : qUnion([Q0]), "oppositeDirection" : true, "depth" : 2 * mm, "offsetDistance" : 25 * mm});
        }
    });
